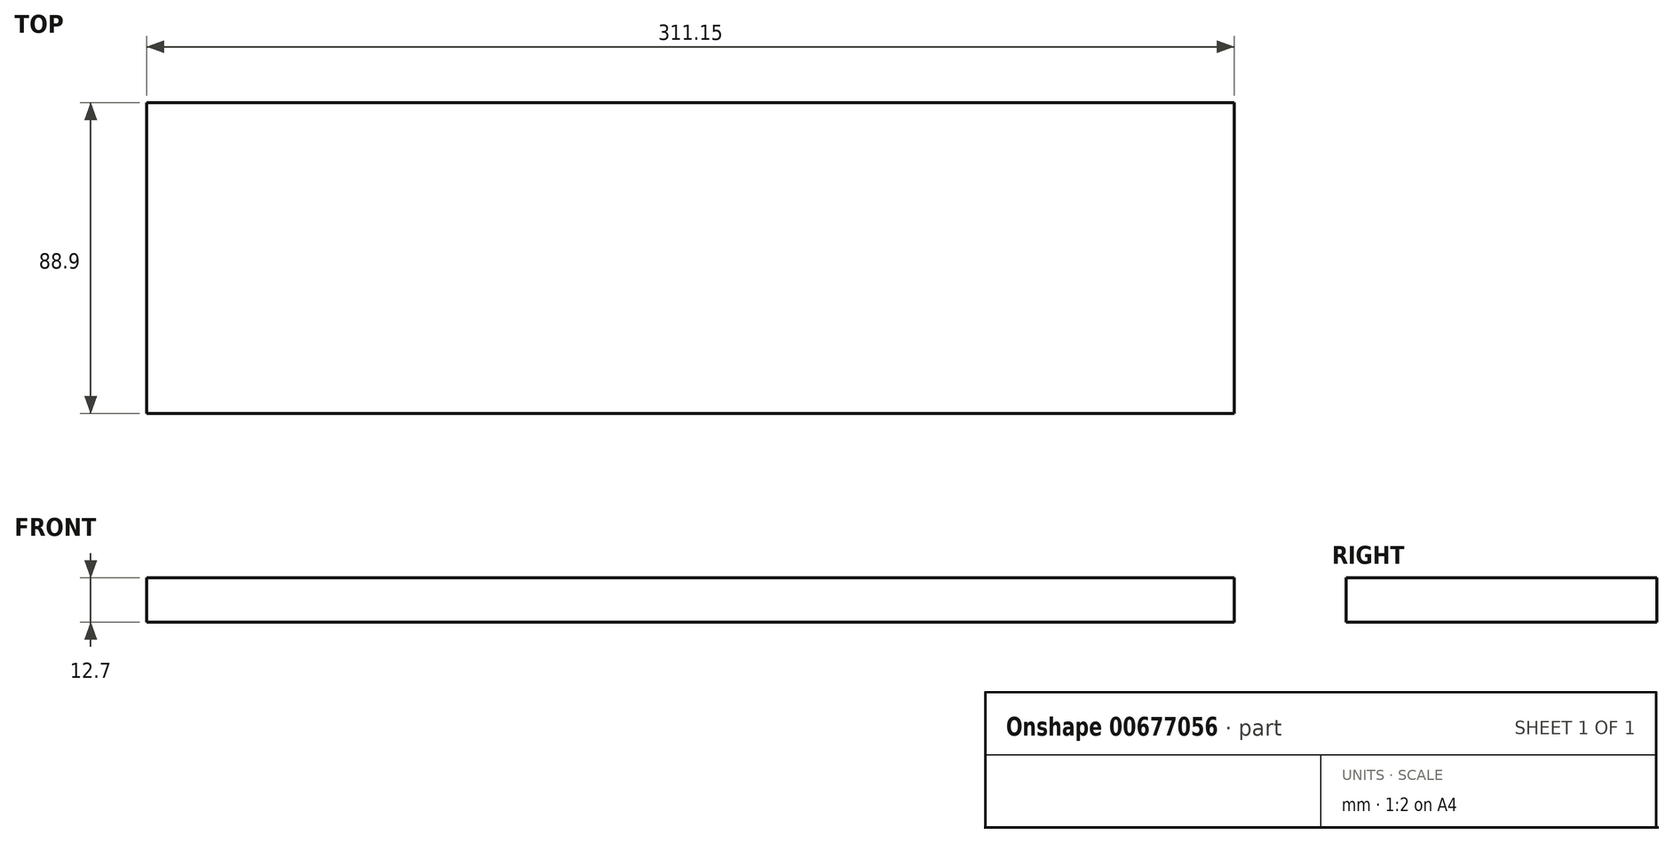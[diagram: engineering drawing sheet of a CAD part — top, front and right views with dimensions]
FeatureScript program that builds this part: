
annotation { "Feature Type Name" : "Feature", "Feature Type Description" : "" }
export const myFeature = defineFeature(function(context is Context, id is Id, definition is map)
    precondition{}
    {
        {
            var Q0;
            Q0=qCreatedBy(makeId("Top.planeOp"),FACE);
            var sketch = newSketch(context, id + "F0", { "sketchPlane" : qUnion([Q0])});
            skLineSegment(sketch, "E0.bottom", {"start": v(-130.47, 28.7) * mm, "end": v(180.68, 28.7) * mm});
            skLineSegment(sketch, "E0.top", {"start": v(-130.47, -60.2) * mm, "end": v(180.68, -60.2) * mm});
            skLineSegment(sketch, "E0.left", {"start": v(-130.47, 28.7) * mm, "end": v(-130.47, -60.2) * mm});
            skLineSegment(sketch, "E0.right", {"start": v(180.68, 28.7) * mm, "end": v(180.68, -60.2) * mm});
            skSolve(sketch);
        }
        {
            var Q0;
            Q0=makeQuery(id+"F0.imprint","IMPRINT",FACE,{"disambiguationData":[TD([[makeQuery(id+"F0.imprint","IMPRINT",EDGE,{"derivedFrom":sQuery(id+"F0.wireOp",EDGE,"E0.bottom")}),-1.0]])]});
            extrude(context, id + "F1", {"entities" : qUnion([Q0]), "depth" : 12.7 * mm, "offsetDistance" : 25.4 * mm});
        }
    });
